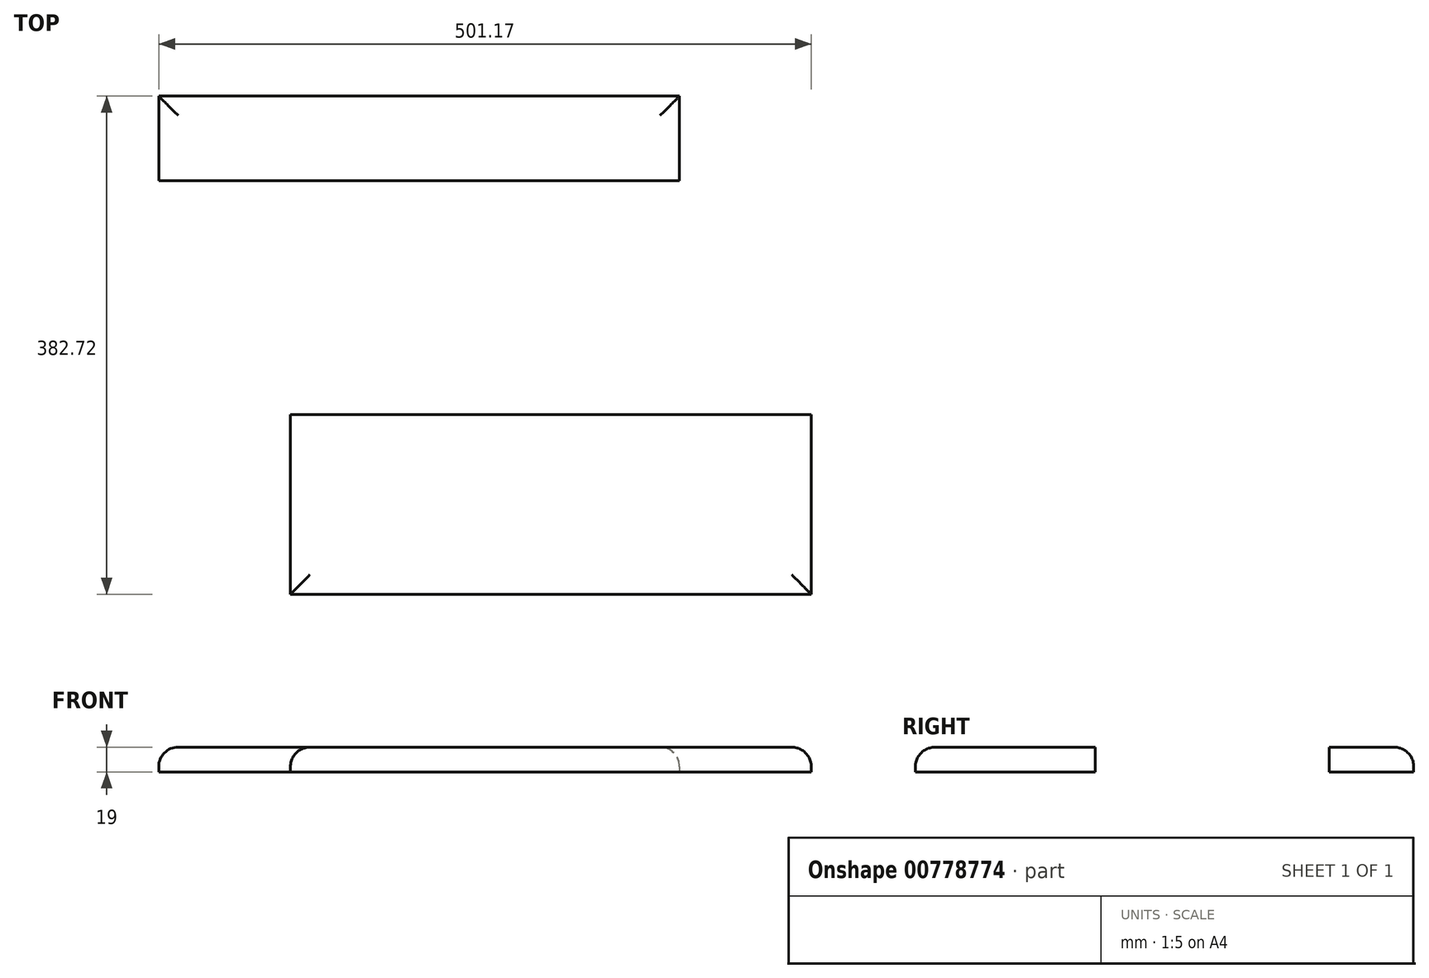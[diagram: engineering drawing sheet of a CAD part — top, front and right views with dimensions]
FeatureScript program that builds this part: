
annotation { "Feature Type Name" : "Feature", "Feature Type Description" : "" }
export const myFeature = defineFeature(function(context is Context, id is Id, definition is map)
    precondition{}
    {
        {
            var Q0;
            Q0=qCreatedBy(makeId("Top.planeOp"),FACE);
            var sketch = newSketch(context, id + "F0", { "sketchPlane" : qUnion([Q0])});
            skLineSegment(sketch, "E0.bottom", {"start": v(-298.83, 65.04) * mm, "end": v(101.17, 65.04) * mm});
            skLineSegment(sketch, "E0.top", {"start": v(-298.83, -72.96) * mm, "end": v(101.17, -72.96) * mm});
            skLineSegment(sketch, "E0.left", {"start": v(-298.83, 65.04) * mm, "end": v(-298.83, -72.96) * mm});
            skLineSegment(sketch, "E0.right", {"start": v(101.17, 65.04) * mm, "end": v(101.17, -72.96) * mm});
            skSolve(sketch);
        }
        {
            var Q0;
            Q0=qCreatedBy(makeId("Top.planeOp"),FACE);
            var sketch = newSketch(context, id + "F1", { "sketchPlane" : qUnion([Q0])});
            skLineSegment(sketch, "E1.bottom", {"start": v(-400, 309.76) * mm, "end": v(0, 309.76) * mm});
            skLineSegment(sketch, "E1.top", {"start": v(-400, 244.76) * mm, "end": v(0, 244.76) * mm});
            skLineSegment(sketch, "E1.left", {"start": v(-400, 309.76) * mm, "end": v(-400, 244.76) * mm});
            skLineSegment(sketch, "E1.right", {"start": v(0, 309.76) * mm, "end": v(0, 244.76) * mm});
            skSolve(sketch);
        }
        {
            var Q0;
            Q0 = qSketchRegion(id + "F1", true);
            extrude(context, id + "F2", {"entities" : qUnion([Q0]), "depth" : 19 * mm, "offsetDistance" : 25 * mm});
        }
        {
            var Q0;
            Q0 = qSketchRegion(id + "F0", true);
            extrude(context, id + "F3", {"entities" : qUnion([Q0]), "depth" : 19 * mm, "offsetDistance" : 25 * mm});
        }
        {
            var Q0;
            Q0=makeQuery(id+"F3.opExtrude","CAP_EDGE",EDGE,{"disambiguationData":[OSD([sQuery(id+"F0.wireOp",EDGE,"E0.top")])],"isStart":false});
            var Q1;
            Q1=makeQuery(id+"F3.opExtrude","CAP_EDGE",EDGE,{"disambiguationData":[OSD([sQuery(id+"F0.wireOp",EDGE,"E0.left")])],"isStart":false});
            var Q2;
            Q2=makeQuery(id+"F3.opExtrude","CAP_EDGE",EDGE,{"disambiguationData":[OSD([sQuery(id+"F0.wireOp",EDGE,"E0.right")])],"isStart":false});
            var Q3;
            Q3=makeQuery(id+"FbXimFZvC3S28zs_0.opExtrude","CAP_EDGE",EDGE,{"disambiguationData":[OSD([sQuery(id+"Fj9DhUIEmFZKbYc_0.wireOp",EDGE,"8acMKumw-ow94-2ptU-EPEk-uYHheAq3cRkj.left")])],"isStart":false});
            var Q4;
            Q4=makeQuery(id+"FbXimFZvC3S28zs_0.opExtrude","CAP_EDGE",EDGE,{"disambiguationData":[OSD([sQuery(id+"Fj9DhUIEmFZKbYc_0.wireOp",EDGE,"8acMKumw-ow94-2ptU-EPEk-uYHheAq3cRkj.right")])],"isStart":false});
            var Q5;
            Q5=makeQuery(id+"F2.opExtrude","CAP_EDGE",EDGE,{"disambiguationData":[OSD([sQuery(id+"F1.wireOp",EDGE,"E1.bottom")])],"isStart":false});
            var Q6;
            Q6=makeQuery(id+"F2.opExtrude","CAP_EDGE",EDGE,{"disambiguationData":[OSD([sQuery(id+"F1.wireOp",EDGE,"E1.left")])],"isStart":false});
            var Q7;
            Q7=makeQuery(id+"F2.opExtrude","CAP_EDGE",EDGE,{"disambiguationData":[OSD([sQuery(id+"F1.wireOp",EDGE,"E1.right")])],"isStart":false});
            fillet(context, id + "F4", {"entities" : qUnion([Q0, Q1, Q2, Q3, Q4, Q5, Q6, Q7]), "radius" : 15 * mm, "tangentPropagation" : true, "allowEdgeOverflow" : false});
        }
    });
